annotation { "Feature Type Name" : "Feature", "Feature Type Description" : "" }
export const myFeature = defineFeature(function(context is Context, id is Id, definition is map)
    precondition{}
    {
        {
            var Q0;
            Q0=qCreatedBy(makeId("Front.planeOp"),FACE);
            var sketch = newSketch(context, id + "F0", { "sketchPlane" : qUnion([Q0])});
            skLineSegment(sketch, "E0.bottom", {"start": v(-96, -96.95) * mm, "end": v(97.62, -96.95) * mm});
            skLineSegment(sketch, "E0.top", {"start": v(-96, 97.22) * mm, "end": v(97.62, 97.22) * mm});
            skLineSegment(sketch, "E0.left", {"start": v(-96, -96.95) * mm, "end": v(-96, 97.22) * mm});
            skLineSegment(sketch, "E0.right", {"start": v(97.62, -96.95) * mm, "end": v(97.62, 97.22) * mm});
            skLineSegment(sketch, "E1", {"start": v(75.86, -76.67) * mm, "end": v(75.86, 77.61) * mm});
            skLineSegment(sketch, "E2", {"start": v(75.86, 77.61) * mm, "end": v(-71.81, 77.61) * mm});
            skLineSegment(sketch, "E3", {"start": v(-71.81, 77.61) * mm, "end": v(-71.81, -75.47) * mm});
            skLineSegment(sketch, "E4", {"start": v(-71.81, -75.47) * mm, "end": v(75.86, -76.67) * mm});
            skLineSegment(sketch, "E5", {"start": v(35.69, -60.23) * mm, "end": v(118.3, 62.27) * mm});
            skLineSegment(sketch, "E6", {"start": v(118.3, 62.27) * mm, "end": v(-34.34, 62.27) * mm});
            skLineSegment(sketch, "E7", {"start": v(-34.34, 62.27) * mm, "end": v(-114.04, -61.13) * mm});
            skLineSegment(sketch, "E8", {"start": v(-114.04, -61.13) * mm, "end": v(35.69, -60.23) * mm});
            skLineSegment(sketch, "E9", {"start": v(-44.86, -141.53) * mm, "end": v(-45.82, 18.22) * mm});
            skLineSegment(sketch, "E10", {"start": v(-45.82, 18.22) * mm, "end": v(42.25, 136.74) * mm});
            skLineSegment(sketch, "E11", {"start": v(42.25, 136.74) * mm, "end": v(42.25, -13.35) * mm});
            skLineSegment(sketch, "E12", {"start": v(42.25, -13.35) * mm, "end": v(-44.86, -141.53) * mm});
            skSolve(sketch);
        }
        {
            var Q0;
            Q0 = qSketchRegion(id + "F0", true);
            extrude(context, id + "F1", {"entities" : qUnion([Q0]), "depth" : 25.4 * mm, "offsetDistance" : 25.4 * mm});
        }
        {
            var Q0;
            Q0=makeQuery(id+"F1.opExtrude","CAP_FACE",FACE,{"disambiguationData":[OSD([sQuery(id+"F0.wireOp",EDGE,"E0.bottom"),sQuery(id+"F0.wireOp",EDGE,"E0.top"),sQuery(id+"F0.wireOp",EDGE,"E0.left"),sQuery(id+"F0.wireOp",EDGE,"E0.right"),sQuery(id+"F0.wireOp",EDGE,"E1"),sQuery(id+"F0.wireOp",EDGE,"E2"),sQuery(id+"F0.wireOp",EDGE,"E3"),sQuery(id+"F0.wireOp",EDGE,"E4"),sQuery(id+"F0.wireOp",EDGE,"E5"),sQuery(id+"F0.wireOp",EDGE,"E6"),sQuery(id+"F0.wireOp",EDGE,"E7"),sQuery(id+"F0.wireOp",EDGE,"E8"),sQuery(id+"F0.wireOp",EDGE,"E9"),sQuery(id+"F0.wireOp",EDGE,"E10"),sQuery(id+"F0.wireOp",EDGE,"E11"),sQuery(id+"F0.wireOp",EDGE,"E12")])],"isStart":true});
            var sketch = newSketch(context, id + "F2", { "sketchPlane" : qUnion([Q0])});
            skLineSegment(sketch, "E13.bottom", {"start": v(-97.62, 97.22) * mm, "end": v(96, 97.22) * mm});
            skLineSegment(sketch, "E13.top", {"start": v(-97.62, -96.95) * mm, "end": v(96, -96.95) * mm});
            skLineSegment(sketch, "E13.left", {"start": v(-97.62, 97.22) * mm, "end": v(-97.62, -96.95) * mm});
            skLineSegment(sketch, "E13.right", {"start": v(96, 97.22) * mm, "end": v(96, -96.95) * mm});
            skSolve(sketch);
        }
        {
            var Q0;
            Q0 = qSketchRegion(id + "F2", true);
            extrude(context, id + "F3", {"entities" : qUnion([Q0]), "operationType" : NewBodyOperationType.ADD, "depth" : 25.4 * mm, "offsetDistance" : 25.4 * mm});
        }
        {
            var Q0;
            Q0=makeQuery(id+"F1.opExtrude","CAP_FACE",FACE,{"disambiguationData":[OSD([sQuery(id+"F0.wireOp",EDGE,"E0.bottom"),sQuery(id+"F0.wireOp",EDGE,"E0.top"),sQuery(id+"F0.wireOp",EDGE,"E0.left"),sQuery(id+"F0.wireOp",EDGE,"E0.right"),sQuery(id+"F0.wireOp",EDGE,"E1"),sQuery(id+"F0.wireOp",EDGE,"E2"),sQuery(id+"F0.wireOp",EDGE,"E3"),sQuery(id+"F0.wireOp",EDGE,"E4"),sQuery(id+"F0.wireOp",EDGE,"E5"),sQuery(id+"F0.wireOp",EDGE,"E6"),sQuery(id+"F0.wireOp",EDGE,"E7"),sQuery(id+"F0.wireOp",EDGE,"E8"),sQuery(id+"F0.wireOp",EDGE,"E9"),sQuery(id+"F0.wireOp",EDGE,"E10"),sQuery(id+"F0.wireOp",EDGE,"E11"),sQuery(id+"F0.wireOp",EDGE,"E12")])],"isStart":false});
            var sketch = newSketch(context, id + "F4", { "sketchPlane" : qUnion([Q0])});
            skLineSegment(sketch, "E14.bottom", {"start": v(-131.34, -135.54) * mm, "end": v(125.9, -135.54) * mm});
            skLineSegment(sketch, "E14.top", {"start": v(-131.34, 134.07) * mm, "end": v(125.9, 134.07) * mm});
            skLineSegment(sketch, "E14.left", {"start": v(-131.34, -135.54) * mm, "end": v(-131.34, 134.07) * mm});
            skLineSegment(sketch, "E14.right", {"start": v(125.9, -135.54) * mm, "end": v(125.9, 134.07) * mm});
            skSolve(sketch);
        }
        {
            var Q0;
            Q0 = qSketchRegion(id + "F4", true);
            extrude(context, id + "F5", {"entities" : qUnion([Q0]), "operationType" : NewBodyOperationType.ADD, "depth" : 1308.77 * mm, "offsetDistance" : 25.4 * mm});
        }
        {
            var Q0;
            Q0=makeQuery(id+"F5.opExtrude","CAP_FACE",FACE,{"disambiguationData":[OSD([sQuery(id+"F4.wireOp",EDGE,"E14.bottom"),sQuery(id+"F4.wireOp",EDGE,"E14.top"),sQuery(id+"F4.wireOp",EDGE,"E14.left"),sQuery(id+"F4.wireOp",EDGE,"E14.right")])],"isStart":false});
            var sketch = newSketch(context, id + "F6", { "sketchPlane" : qUnion([Q0])});
            skLineSegment(sketch, "E15.bottom", {"start": v(-248, -243) * mm, "end": v(206.86, -243) * mm});
            skLineSegment(sketch, "E15.top", {"start": v(-248, 130.85) * mm, "end": v(206.86, 130.85) * mm});
            skLineSegment(sketch, "E15.left", {"start": v(-248, -243) * mm, "end": v(-248, 130.85) * mm});
            skLineSegment(sketch, "E15.right", {"start": v(206.86, -243) * mm, "end": v(206.86, 130.85) * mm});
            skSolve(sketch);
        }
        {
            var Q0;
            Q0 = qSketchRegion(id + "F6", true);
            extrude(context, id + "F7", {"entities" : qUnion([Q0]), "operationType" : NewBodyOperationType.ADD, "depth" : 343.05 * mm, "offsetDistance" : 25.4 * mm});
        }
        {
            var Q0;
            Q0=makeQuery(id+"F7.opExtrude","SWEPT_FACE",FACE,{"disambiguationData":[OSD([sQuery(id+"F6.wireOp",EDGE,"E15.top")])]});
            var sketch = newSketch(context, id + "F8", { "sketchPlane" : qUnion([Q0])});
            skLineSegment(sketch, "E16.bottom", {"start": v(-269.38, -1256.89) * mm, "end": v(206.86, -1256.89) * mm});
            skLineSegment(sketch, "E16.top", {"start": v(-269.38, -1551.95) * mm, "end": v(206.86, -1551.95) * mm});
            skLineSegment(sketch, "E16.left", {"start": v(-269.38, -1256.89) * mm, "end": v(-269.38, -1551.95) * mm});
            skLineSegment(sketch, "E16.right", {"start": v(206.86, -1256.89) * mm, "end": v(206.86, -1551.95) * mm});
            skLineSegment(sketch, "E17.bottom", {"start": v(-269.38, -1551.95) * mm, "end": v(134.46, -1551.95) * mm});
            skLineSegment(sketch, "E17.top", {"start": v(-269.38, -1720.21) * mm, "end": v(134.46, -1720.21) * mm});
            skLineSegment(sketch, "E17.left", {"start": v(-269.38, -1551.95) * mm, "end": v(-269.38, -1720.21) * mm});
            skLineSegment(sketch, "E17.right", {"start": v(134.46, -1551.95) * mm, "end": v(134.46, -1720.21) * mm});
            skLineSegment(sketch, "E18.bottom", {"start": v(134.46, -1573.87) * mm, "end": v(206.86, -1573.87) * mm});
            skLineSegment(sketch, "E18.top", {"start": v(134.46, -1583.53) * mm, "end": v(206.86, -1583.53) * mm});
            skLineSegment(sketch, "E18.left", {"start": v(134.46, -1573.87) * mm, "end": v(134.46, -1583.53) * mm});
            skLineSegment(sketch, "E18.right", {"start": v(206.86, -1573.87) * mm, "end": v(206.86, -1583.53) * mm});
            skSolve(sketch);
        }
        {
            var Q0;
            Q0 = qSketchRegion(id + "F8", true);
            extrude(context, id + "F9", {"entities" : qUnion([Q0]), "operationType" : NewBodyOperationType.ADD, "depth" : 2631.33 * mm, "offsetDistance" : 25.4 * mm});
        }
        {
            var Q0;
            Q0=makeQuery(id+"F9.opExtrude","CAP_FACE",FACE,{"disambiguationData":[OSD([sQuery(id+"F8.wireOp",EDGE,"E16.bottom"),sQuery(id+"F8.wireOp",EDGE,"E16.top"),sQuery(id+"F8.wireOp",EDGE,"E16.left"),sQuery(id+"F8.wireOp",EDGE,"E16.right"),sQuery(id+"F8.wireOp",EDGE,"E17.top"),sQuery(id+"F8.wireOp",EDGE,"E17.left"),sQuery(id+"F8.wireOp",EDGE,"E17.right"),sQuery(id+"F8.wireOp",EDGE,"E18.bottom"),sQuery(id+"F8.wireOp",EDGE,"E18.top"),sQuery(id+"F8.wireOp",EDGE,"E18.right")])],"isStart":false});
            var sketch = newSketch(context, id + "F10", { "sketchPlane" : qUnion([Q0])});
            skLineSegment(sketch, "E19.bottom", {"start": v(-539.3, -976.64) * mm, "end": v(481.37, -976.64) * mm});
            skLineSegment(sketch, "E19.top", {"start": v(-539.3, -1997.26) * mm, "end": v(481.37, -1997.26) * mm});
            skLineSegment(sketch, "E19.left", {"start": v(-539.3, -976.64) * mm, "end": v(-539.3, -1997.26) * mm});
            skLineSegment(sketch, "E19.right", {"start": v(481.37, -976.64) * mm, "end": v(481.37, -1997.26) * mm});
            skLineSegment(sketch, "E20.bottom", {"start": v(0, -1514.56) * mm, "end": v(-269.38, -1514.56) * mm});
            skLineSegment(sketch, "E20.top", {"start": v(0, -1256.89) * mm, "end": v(-269.38, -1256.89) * mm});
            skLineSegment(sketch, "E20.left", {"start": v(0, -1514.56) * mm, "end": v(0, -1256.89) * mm});
            skLineSegment(sketch, "E20.right", {"start": v(-269.38, -1514.56) * mm, "end": v(-269.38, -1256.89) * mm});
            skSolve(sketch);
        }
        {
            var Q0;
            Q0 = qSketchRegion(id + "F10", true);
            extrude(context, id + "F11", {"entities" : qUnion([Q0]), "operationType" : NewBodyOperationType.ADD, "oppositeDirection" : true, "depth" : 5103.79 * mm, "offsetDistance" : 25.4 * mm});
        }
        {
            var Q0;
            Q0=makeQuery(id+"F11.boolean.opBoolean","MERGE",FACE,{"derivedFrom":[makeQuery(id+"F9.opExtrude","CAP_FACE",FACE,{"disambiguationData":[OSD([sQuery(id+"F8.wireOp",EDGE,"E16.bottom"),sQuery(id+"F8.wireOp",EDGE,"E16.top"),sQuery(id+"F8.wireOp",EDGE,"E16.left"),sQuery(id+"F8.wireOp",EDGE,"E16.right"),sQuery(id+"F8.wireOp",EDGE,"E17.top"),sQuery(id+"F8.wireOp",EDGE,"E17.left"),sQuery(id+"F8.wireOp",EDGE,"E17.right"),sQuery(id+"F8.wireOp",EDGE,"E18.bottom"),sQuery(id+"F8.wireOp",EDGE,"E18.top"),sQuery(id+"F8.wireOp",EDGE,"E18.right")])],"isStart":false}),makeQuery(id+"F11.opExtrude","CAP_FACE",FACE,{"disambiguationData":[OSD([sQuery(id+"F10.wireOp",EDGE,"E19.bottom"),sQuery(id+"F10.wireOp",EDGE,"E19.top"),sQuery(id+"F10.wireOp",EDGE,"E19.left"),sQuery(id+"F10.wireOp",EDGE,"E19.right"),sQuery(id+"F10.wireOp",EDGE,"E20.bottom"),sQuery(id+"F10.wireOp",EDGE,"E20.top"),sQuery(id+"F10.wireOp",EDGE,"E20.left"),sQuery(id+"F10.wireOp",EDGE,"E20.right")])],"isStart":true})]});
            var sketch = newSketch(context, id + "F12", { "sketchPlane" : qUnion([Q0])});
            skLineSegment(sketch, "E21.bottom", {"start": v(1140.5, -2662.38) * mm, "end": v(-1200.13, -2662.38) * mm});
            skLineSegment(sketch, "E21.top", {"start": v(1140.5, -334.92) * mm, "end": v(-1200.13, -334.92) * mm});
            skLineSegment(sketch, "E21.left", {"start": v(1140.5, -2662.38) * mm, "end": v(1140.5, -334.92) * mm});
            skLineSegment(sketch, "E21.right", {"start": v(-1200.13, -2662.38) * mm, "end": v(-1200.13, -334.92) * mm});
            skLineSegment(sketch, "E22.bottom", {"start": v(-539.3, -1997.26) * mm, "end": v(481.37, -1997.26) * mm});
            skLineSegment(sketch, "E22.top", {"start": v(-539.3, -976.64) * mm, "end": v(481.37, -976.64) * mm});
            skLineSegment(sketch, "E22.left", {"start": v(-539.3, -1997.26) * mm, "end": v(-539.3, -976.64) * mm});
            skLineSegment(sketch, "E22.right", {"start": v(481.37, -1997.26) * mm, "end": v(481.37, -976.64) * mm});
            skSolve(sketch);
        }
        {
            var Q0;
            Q0 = qSketchRegion(id + "F12", true);
            extrude(context, id + "F13", {"entities" : qUnion([Q0]), "depth" : 7168.64 * mm, "offsetDistance" : 25.4 * mm});
        }
        {
            var Q0;
            Q0=makeQuery(id+"F13.opExtrude","SWEPT_FACE",FACE,{"disambiguationData":[OSD([sQuery(id+"F12.wireOp",EDGE,"E21.right")])]});
            var sketch = newSketch(context, id + "F14", { "sketchPlane" : qUnion([Q0])});
            skLineSegment(sketch, "E23.bottom", {"start": v(-1987.43, 9783.4) * mm, "end": v(6615.47, 9783.4) * mm});
            skLineSegment(sketch, "E23.top", {"start": v(-1987.43, 1882.88) * mm, "end": v(6615.47, 1882.88) * mm});
            skLineSegment(sketch, "E23.left", {"start": v(-1987.43, 9783.4) * mm, "end": v(-1987.43, 1882.88) * mm});
            skLineSegment(sketch, "E23.right", {"start": v(6615.47, 9783.4) * mm, "end": v(6615.47, 1882.88) * mm});
            skSolve(sketch);
        }
        {
            var Q0;
            Q0 = qSketchRegion(id + "F14", true);
            extrude(context, id + "F15", {"entities" : qUnion([Q0]), "operationType" : NewBodyOperationType.ADD, "depth" : 20199.43 * mm, "offsetDistance" : 25.4 * mm});
        }
        {
            var Q0;
            Q0=makeQuery(id+"F11.opExtrude","SWEPT_FACE",FACE,{"disambiguationData":[OSD([sQuery(id+"F10.wireOp",EDGE,"E19.top")])]});
            var sketch = newSketch(context, id + "F16", { "sketchPlane" : qUnion([Q0])});
            skLineSegment(sketch, "E24.bottom", {"start": v(-5714.1, 5899.05) * mm, "end": v(5752.92, 5899.05) * mm});
            skLineSegment(sketch, "E24.top", {"start": v(-5714.1, -6049.75) * mm, "end": v(5752.92, -6049.75) * mm});
            skLineSegment(sketch, "E24.left", {"start": v(-5714.1, 5899.05) * mm, "end": v(-5714.1, -6049.75) * mm});
            skLineSegment(sketch, "E24.right", {"start": v(5752.92, 5899.05) * mm, "end": v(5752.92, -6049.75) * mm});
            skLineSegment(sketch, "E25.bottom", {"start": v(-4388.88, 0) * mm, "end": v(4579.26, 0) * mm});
            skLineSegment(sketch, "E25.top", {"start": v(-4388.88, 4529.09) * mm, "end": v(4579.26, 4529.09) * mm});
            skLineSegment(sketch, "E25.left", {"start": v(-4388.88, 0) * mm, "end": v(-4388.88, 4529.09) * mm});
            skLineSegment(sketch, "E25.right", {"start": v(4579.26, 0) * mm, "end": v(4579.26, 4529.09) * mm});
            skSolve(sketch);
        }
        {
            var Q0;
            Q0 = qSketchRegion(id + "F16", true);
            extrude(context, id + "F17", {"entities" : qUnion([Q0]), "depth" : 29000.42 * mm, "offsetDistance" : 25.4 * mm});
        }
        {
            var Q0;
            Q0=makeQuery(id+"F15.opExtrude","SWEPT_FACE",FACE,{"disambiguationData":[OSD([sQuery(id+"F14.wireOp",EDGE,"E23.left")])]});
            var sketch = newSketch(context, id + "F18", { "sketchPlane" : qUnion([Q0])});
            skLineSegment(sketch, "E26.bottom", {"start": v(7131.08, -7710.56) * mm, "end": v(-3275.97, -7710.56) * mm});
            skLineSegment(sketch, "E26.top", {"start": v(7131.08, 705.23) * mm, "end": v(-3275.97, 705.23) * mm});
            skLineSegment(sketch, "E26.left", {"start": v(7131.08, -7710.56) * mm, "end": v(7131.08, 705.23) * mm});
            skLineSegment(sketch, "E26.right", {"start": v(-3275.97, -7710.56) * mm, "end": v(-3275.97, 705.23) * mm});
            skSolve(sketch);
        }
        {
            var Q0;
            Q0 = qSketchRegion(id + "F18", true);
            extrude(context, id + "F19", {"entities" : qUnion([Q0]), "depth" : 25.4 * mm, "offsetDistance" : 25.4 * mm});
        }
        {
            var Q0;
            Q0=makeQuery(id+"F17.opExtrude","CAP_FACE",FACE,{"disambiguationData":[OSD([sQuery(id+"F16.wireOp",EDGE,"E24.bottom"),sQuery(id+"F16.wireOp",EDGE,"E24.top"),sQuery(id+"F16.wireOp",EDGE,"E24.left"),sQuery(id+"F16.wireOp",EDGE,"E24.right"),sQuery(id+"F16.wireOp",EDGE,"E25.bottom"),sQuery(id+"F16.wireOp",EDGE,"E25.top"),sQuery(id+"F16.wireOp",EDGE,"E25.left"),sQuery(id+"F16.wireOp",EDGE,"E25.right")])],"isStart":false});
            extrude(context, id + "F20", {"entities" : qUnion([Q0]), "operationType" : NewBodyOperationType.ADD, "depth" : 35806.3 * mm, "offsetDistance" : 25.4 * mm});
        }
        {
            var Q0;
            Q0=makeQuery(id+"F17.opExtrude","CAP_FACE",FACE,{"disambiguationData":[OSD([sQuery(id+"F16.wireOp",EDGE,"E24.bottom"),sQuery(id+"F16.wireOp",EDGE,"E24.top"),sQuery(id+"F16.wireOp",EDGE,"E24.left"),sQuery(id+"F16.wireOp",EDGE,"E24.right"),sQuery(id+"F16.wireOp",EDGE,"E25.bottom"),sQuery(id+"F16.wireOp",EDGE,"E25.top"),sQuery(id+"F16.wireOp",EDGE,"E25.left"),sQuery(id+"F16.wireOp",EDGE,"E25.right")])],"isStart":true});
            var sketch = newSketch(context, id + "F21", { "sketchPlane" : qUnion([Q0])});
            skLineSegment(sketch, "E27.bottom", {"start": v(10863.64, -11030.91) * mm, "end": v(-10870.6, -11030.91) * mm});
            skLineSegment(sketch, "E27.top", {"start": v(10863.64, 10593.62) * mm, "end": v(-10870.6, 10593.62) * mm});
            skLineSegment(sketch, "E27.left", {"start": v(10863.64, -11030.91) * mm, "end": v(10863.64, 10593.62) * mm});
            skLineSegment(sketch, "E27.right", {"start": v(-10870.6, -11030.91) * mm, "end": v(-10870.6, 10593.62) * mm});
            skSolve(sketch);
        }
        {
            var Q0;
            Q0 = qSketchRegion(id + "F21", true);
            extrude(context, id + "F22", {"entities" : qUnion([Q0]), "depth" : 25.4 * mm, "offsetDistance" : 25.4 * mm});
        }
        {
            var Q0;
            {var subQ0=sQuery(id+"F16.wireOp",EDGE,"E24.top");Q0=makeQuery(id+"F20.boolean.opBoolean","MERGE",FACE,{"derivedFrom":[makeQuery(id+"F17.opExtrude","SWEPT_FACE",FACE,{"disambiguationData":[OSD([subQ0])]}),makeQuery(id+"F20.opExtrude","SWEPT_FACE",FACE,{"disambiguationData":[OSD([subQ0])]})]});}
            var sketch = newSketch(context, id + "F23", { "sketchPlane" : qUnion([Q0])});
            skLineSegment(sketch, "E28.bottom", {"start": v(-24552.94, 4747.74) * mm, "end": v(14219.65, 4747.74) * mm});
            skLineSegment(sketch, "E28.top", {"start": v(-24552.94, 66685.88) * mm, "end": v(14219.65, 66685.88) * mm});
            skLineSegment(sketch, "E28.left", {"start": v(-24552.94, 4747.74) * mm, "end": v(-24552.94, 66685.88) * mm});
            skLineSegment(sketch, "E28.right", {"start": v(14219.65, 4747.74) * mm, "end": v(14219.65, 66685.88) * mm});
            skSolve(sketch);
        }
        {
            var Q0;
            Q0 = qSketchRegion(id + "F23", true);
            extrude(context, id + "F24", {"entities" : qUnion([Q0]), "operationType" : NewBodyOperationType.ADD, "depth" : 25.4 * mm, "offsetDistance" : 25.4 * mm});
        }
        {
            var Q0;
            {var subQ0=sQuery(id+"F16.wireOp",EDGE,"E24.left");Q0=makeQuery(id+"F20.boolean.opBoolean","MERGE",FACE,{"derivedFrom":[makeQuery(id+"F17.opExtrude","SWEPT_FACE",FACE,{"disambiguationData":[OSD([subQ0])]}),makeQuery(id+"F20.opExtrude","SWEPT_FACE",FACE,{"disambiguationData":[OSD([subQ0])]})]});}
            var sketch = newSketch(context, id + "F25", { "sketchPlane" : qUnion([Q0])});
            skLineSegment(sketch, "E29.bottom", {"start": v(68173.03, -34021.93) * mm, "end": v(0, -34021.93) * mm});
            skLineSegment(sketch, "E29.top", {"start": v(68173.03, 33222.4) * mm, "end": v(0, 33222.4) * mm});
            skLineSegment(sketch, "E29.left", {"start": v(68173.03, -34021.93) * mm, "end": v(68173.03, 33222.4) * mm});
            skLineSegment(sketch, "E29.right", {"start": v(0, -34021.93) * mm, "end": v(0, 33222.4) * mm});
            skSolve(sketch);
        }
        {
            var Q0;
            Q0 = qSketchRegion(id + "F25", true);
            extrude(context, id + "F26", {"entities" : qUnion([Q0]), "depth" : 247647.45 * mm, "offsetDistance" : 25.4 * mm});
        }
        {
            var Q0;
            Q0=makeQuery(id+"F26.opExtrude","SWEPT_FACE",FACE,{"disambiguationData":[OSD([sQuery(id+"F25.wireOp",EDGE,"E29.bottom")])]});
            var sketch = newSketch(context, id + "F27", { "sketchPlane" : qUnion([Q0])});
            skLineSegment(sketch, "E30.bottom", {"start": v(-5714.1, 68173.03) * mm, "end": v(117366.9, 68173.03) * mm});
            skLineSegment(sketch, "E30.top", {"start": v(-5714.1, 8974.7) * mm, "end": v(117366.9, 8974.7) * mm});
            skLineSegment(sketch, "E30.left", {"start": v(-5714.1, 68173.03) * mm, "end": v(-5714.1, 8974.7) * mm});
            skLineSegment(sketch, "E30.right", {"start": v(117366.9, 68173.03) * mm, "end": v(117366.9, 8974.7) * mm});
            skLineSegment(sketch, "E31.bottom", {"start": v(117366.9, 8974.7) * mm, "end": v(41140.56, 8974.7) * mm});
            skLineSegment(sketch, "E31.top", {"start": v(117366.9, -14883.15) * mm, "end": v(41140.56, -14883.15) * mm});
            skLineSegment(sketch, "E31.left", {"start": v(117366.9, 8974.7) * mm, "end": v(117366.9, -14883.15) * mm});
            skLineSegment(sketch, "E31.right", {"start": v(41140.56, 8974.7) * mm, "end": v(41140.56, -14883.15) * mm});
            skLineSegment(sketch, "E32.bottom", {"start": v(41140.56, 53840.85) * mm, "end": v(117366.9, 53840.85) * mm});
            skLineSegment(sketch, "E32.top", {"start": v(41140.56, -8792.92) * mm, "end": v(117366.9, -8792.92) * mm});
            skLineSegment(sketch, "E32.left", {"start": v(41140.56, 53840.85) * mm, "end": v(41140.56, -8792.92) * mm});
            skLineSegment(sketch, "E32.right", {"start": v(117366.9, 53840.85) * mm, "end": v(117366.9, -8792.92) * mm});
            skLineSegment(sketch, "E33.bottom", {"start": v(-5714.1, 0) * mm, "end": v(117366.9, 0) * mm});
            skLineSegment(sketch, "E33.left", {"start": v(-5714.1, 0) * mm, "end": v(-5714.1, 8974.7) * mm});
            skLineSegment(sketch, "E33.right", {"start": v(117366.9, 0) * mm, "end": v(117366.9, 8974.7) * mm});
            skSolve(sketch);
        }
        {
            var Q0;
            Q0 = qSketchRegion(id + "F27", true);
            extrude(context, id + "F28", {"entities" : qUnion([Q0]), "depth" : 297722.8 * mm, "offsetDistance" : 25.4 * mm});
        }
        {
            var Q0;
            Q0=makeQuery(id+"F28.opExtrude","CAP_FACE",FACE,{"disambiguationData":[OSD([sQuery(id+"F27.wireOp",EDGE,"E30.bottom"),sQuery(id+"F27.wireOp",EDGE,"E30.left"),sQuery(id+"F27.wireOp",EDGE,"E30.right"),sQuery(id+"F27.wireOp",EDGE,"E31.top"),sQuery(id+"F27.wireOp",EDGE,"E31.left"),sQuery(id+"F27.wireOp",EDGE,"E31.right"),sQuery(id+"F27.wireOp",EDGE,"E32.left"),sQuery(id+"F27.wireOp",EDGE,"E32.right"),sQuery(id+"F27.wireOp",EDGE,"E33.bottom"),sQuery(id+"F27.wireOp",EDGE,"E33.left"),sQuery(id+"F27.wireOp",EDGE,"E33.right")])],"isStart":false});
            var sketch = newSketch(context, id + "F29", { "sketchPlane" : qUnion([Q0])});
            skLineSegment(sketch, "E34.bottom", {"start": v(-132502.26, -156803.05) * mm, "end": v(244401.61, -156803.05) * mm});
            skLineSegment(sketch, "E34.top", {"start": v(-132502.26, 217594.5) * mm, "end": v(244401.61, 217594.5) * mm});
            skLineSegment(sketch, "E34.left", {"start": v(-132502.26, -156803.05) * mm, "end": v(-132502.26, 217594.5) * mm});
            skLineSegment(sketch, "E34.right", {"start": v(244401.61, -156803.05) * mm, "end": v(244401.61, 217594.5) * mm});
            skLineSegment(sketch, "E35.bottom", {"start": v(-368486.27, 41266.22) * mm, "end": v(-132502.26, 41266.22) * mm});
            skLineSegment(sketch, "E35.top", {"start": v(-368486.27, 0) * mm, "end": v(-132502.26, 0) * mm});
            skLineSegment(sketch, "E35.left", {"start": v(-368486.27, 41266.22) * mm, "end": v(-368486.27, 0) * mm});
            skLineSegment(sketch, "E35.right", {"start": v(-132502.26, 41266.22) * mm, "end": v(-132502.26, 0) * mm});
            skSolve(sketch);
        }
        {
            var Q0;
            Q0 = qSketchRegion(id + "F29", true);
            extrude(context, id + "F30", {"entities" : qUnion([Q0]), "oppositeDirection" : true, "depth" : 440830.6 * mm, "offsetDistance" : 25.4 * mm});
        }
        {
            var Q0;
            Q0=makeQuery(id+"F30.opExtrude","CAP_FACE",FACE,{"disambiguationData":[OSD([sQuery(id+"F29.wireOp",EDGE,"E34.bottom"),sQuery(id+"F29.wireOp",EDGE,"E34.top"),sQuery(id+"F29.wireOp",EDGE,"E34.left"),sQuery(id+"F29.wireOp",EDGE,"E34.right"),sQuery(id+"F29.wireOp",EDGE,"E35.bottom"),sQuery(id+"F29.wireOp",EDGE,"E35.top"),sQuery(id+"F29.wireOp",EDGE,"E35.left")])],"isStart":true});
            extrude(context, id + "F31", {"entities" : qUnion([Q0]), "oppositeDirection" : true, "depth" : 419155.18 * mm, "offsetDistance" : 25.4 * mm});
        }
        {
            var Q0;
            Q0=makeQuery(id+"F30.opExtrude","CAP_FACE",FACE,{"disambiguationData":[OSD([sQuery(id+"F29.wireOp",EDGE,"E34.bottom"),sQuery(id+"F29.wireOp",EDGE,"E34.top"),sQuery(id+"F29.wireOp",EDGE,"E34.left"),sQuery(id+"F29.wireOp",EDGE,"E34.right"),sQuery(id+"F29.wireOp",EDGE,"E35.bottom"),sQuery(id+"F29.wireOp",EDGE,"E35.top"),sQuery(id+"F29.wireOp",EDGE,"E35.left")])],"isStart":false});
            var sketch = newSketch(context, id + "F32", { "sketchPlane" : qUnion([Q0])});
            skLineSegment(sketch, "E36.bottom", {"start": v(-354359.1, 268680.51) * mm, "end": v(239323.91, 268680.51) * mm});
            skLineSegment(sketch, "E36.top", {"start": v(-354359.1, -424392.06) * mm, "end": v(239323.91, -424392.06) * mm});
            skLineSegment(sketch, "E36.left", {"start": v(-354359.1, 268680.51) * mm, "end": v(-354359.1, -424392.06) * mm});
            skLineSegment(sketch, "E36.right", {"start": v(239323.91, 268680.51) * mm, "end": v(239323.91, -424392.06) * mm});
            skSolve(sketch);
        }
        {
            var Q0;
            Q0 = qSketchRegion(id + "F32", true);
            extrude(context, id + "F33", {"entities" : qUnion([Q0]), "operationType" : NewBodyOperationType.ADD, "depth" : 25.4 * mm, "offsetDistance" : 25.4 * mm});
        }
    });